# Revit family: BE_77264_de_DE
name_source: partatom
category: Lighting Fixtures
revit_build: Autodesk Revit 2015 (Build: 20160512_0715(x64)
units: mm (PartAtom-declared; Revit-internal decimal feet)

## types (2) — shared parameters
AC/DC = AC/DC
Aktualisierung = 2017-04-12T04:17:31
Apparent Load = 0 VA
BEGA_Dummy = No
BEGA_IES = Yes
BEGA_Intern = Yes
BEGA_Intern_Konstruktion = Yes
BEGA_Intern_an = Yes
BEGA_Intern_aus = Yes
Beschreibung_Sonderanfertigung = Hier können Sie Informationen zur Sonderanfertigung eintragen.
CE_Konformität = ja
Color Filter = 16777215
Description = Garten- und Wegeleuchte
Dimming Lamp Color Temperature Shift = <None>
ENEC = ja
Energieeffizienzklasse = LED A++ - A
Farbtemperatur = 3000 K
Farbwiedergabeindex = Ra > 80
Frequenz = 0/50-60 Hz
Gewicht = 2.4 kg
LED_Modulbezeichnung = LED-0234/80
Lamp = LED 2.1 W
Lampenlichtstrom = 280 lm
Lastklassifizierung = Beleuchtung
Lebensdauerkriterien = L70 = 50.000 h
Leuchtenlichtstrom = 143 lm
Logo = BEGA_Logo.png
Manufacturer = BEGA
Material_02 = BEGA_Oberfläche_Silber_matt
Material_03 = BEGA_Oberfläche_Weiss_matt
Material_06 = BEGA_Oberfläche_Edelstahl_gebürstet
Material_09 = BEGA_Glas_klar
Material_10 = BEGA_Glas_opal
Material_11 = BEGA_Glas_opal
Material_15 = BEGA_Leuchtmedium_matt
Material_17 = BEGA_Reflektor
Photometric Web File = BE_77264.IES
Produktdatenblatt = http://www.bega.de
Schutzart = IP 65
Schutzklasse = I
Sonderanfertigung = No
Spannung = 240 V
Tilt Angle = 0.00°
Type Image = 77264.png
URL = http://www.bega.de
Umgebungstemperatur = 25 °C
zero-valued in all types: Default Elevation

## per-type parameters (varying)
| type | Bestellnummer | M_A | M_G | Model |
| BEGA_77264_Silber_K3 | 77264A | Yes | No | 77264A |
| BEGA_77264_Grafit_K3 | 77264 | No | Yes | 77264 |
